# Revit family: TY3332
name_source: partatom
category: Sprinklers
revit_build: Autodesk Revit 2016 (Build: 20150220_1215(x64)
units: mm (PartAtom-declared; Revit-internal decimal feet)

## family parameters
Always vertical = Yes
Cut with Voids When Loaded = No
Maintain Annotation Orientation = No
OmniClass Number = 23.65.70.17.11.24
OmniClass Title = Fire Fighting Sprinkler Heads
Part Type = Normal
Room Calculation Point = No
Round Connector Dimension = Use Diameter
Shared = No
Work Plane-Based = No

## types (15) — shared parameters
COBie = Yes
COBie.Component.Name = Sprinklers:Sidewall_SIN
COBie.Type = Yes
COBie.Type.AssetType = Fixed
COBie.Type.Category = Pr_70_55_97_84:Sprinklers
COBie.Type.Manufacturer = Tyco Fire Protection Products
COBie.Type.Material = Bronze
COBie.Type.NominalHeight = 0' - 0"
COBie.Type.NominalLength = 0' - 0"
COBie.Type.NominalWidth = 0' - 0"
COBie.Type.Shape = Cylinder
COBie.Type.Size = 1/2"(DN15)
COBie.Type.WarrantyGuarantorParts = http://tycofsbp.com
Coverage = Extended
Coverage_ = Extended
K-Factor = 5.5493
Manufacturer = Tyco Fire Protection Products
Manufacturer URL = www.tyco-fire.com
Material_ = Bronze
Model = TY-FRB
Nominal Diameter 1 = 1"
Orifice = Standard
Orifice Size = 0"
Outside Diameter 1 = 1"
Response = Quick
Response_ = Quick
SIN No = TY3332
Takeout 1 = 2"
Technical Data Sheet No = TFP296
zero-valued in all types: COBie.Type.ReplacementCost, Style Id

## per-type parameters (varying)
| type | COBie.Component.Description | COBie.Type.Colour | COBie.Type.DurationUnit | COBie.Type.Finish | COBie.Type.ModelNumber | COBie.Type.ModelReference | Description | Finish_ | Part No | Temperature Rating |
| Horizontal Sidewall Brass 135°F 5.6K ½" NPT_57-376-1-135 | TY-FRB Wet Sidewall  57.2°C K80 DN15 NPT Br | Yellow | year | Natural Brass | 57-376-1-135 | TY-FRB Wet Sidewall  57.2°C K80 DN15 NPT Br | TY-FRB Horizontal Sidewall Brass 135°F 5.6K ½" NPT_57-376-1-135 | Natural Brass | 57-376-1-135 | 135 °F |
| Horizontal Sidewall Brass 155°F 5.6K ½" NPT_57-376-1-155 | TY-FRB Wet Sidewall  68.3°C K80 DN15 NPT Br | Yellow | year | Natural Brass | 57-376-1-155 | TY-FRB Wet Sidewall  68.3°C K80 DN15 NPT Br | TY-FRB Horizontal Sidewall Brass 155°F 5.6K ½" NPT_57-376-1-155 | Natural Brass | 57-376-1-155 | 155 °F |
| Horizontal Sidewall Brass 175°F 5.6K ½" NPT_57-376-1-175 | TY-FRB Wet Sidewall  79.4°C K80 DN15 NPT Br | Yellow | year | Natural Brass | 57-376-1-175 | TY-FRB Wet Sidewall  79.4°C K80 DN15 NPT Br | TY-FRB Horizontal Sidewall Brass 175°F 5.6K ½" NPT_57-376-1-175 | Natural Brass | 57-376-1-175 | 175 °F |
| Horizontal Sidewall White 9010 135°F 5.6K ½" NPT_57-376-3-135 | TY-FRB Wet Sidewall  57.2°C K80 DN15 NPT Wh9010 | White | year | Pure White | 57-376-3-135 | TY-FRB Wet Sidewall  57.2°C K80 DN15 NPT Wh9010 | TY-FRB Horizontal Sidewall White 9010 135°F 5.6K ½" NPT_57-376-3-135 | White RAL9010 | 57-376-3-135 | 135 °F |
| Horizontal Sidewall White 9010 155°F 5.6K ½" NPT_57-376-3-155 | TY-FRB Wet Sidewall  68.3°C K80 DN15 NPT Wh9010 | White |  | Pure White | 57-376-3-155 | TY-FRB Wet Sidewall  68.3°C K80 DN15 NPT Wh9010 | TY-FRB Horizontal Sidewall White 9010 155°F 5.6K ½" NPT_57-376-3-155 | White RAL9010 | 57-376-3-155 | 155 °F |
| Horizontal Sidewall White 9010 175°F 5.6K ½" NPT_57-376-3-175 | TY-FRB Wet Sidewall  79.4°C K80 DN15 NPT Wh9010 | White | year | Pure White | 57-376-3-175 | TY-FRB Wet Sidewall  79.4°C K80 DN15 NPT Wh9010 | TY-FRB Horizontal Sidewall White 9010 175°F 5.6K ½" NPT_57-376-3-175 | White RAL9010 | 57-376-3-175 | 175 °F |
| Horizontal Sidewall White 135°F 5.6K ½" NPT_57-376-4-135 | TY-FRB Wet Sidewall  57.2°C K80 DN15 NPT Wh9003 | White | year | Signal White | 57-376-4-135 | TY-FRB Wet Sidewall  57.2°C K80 DN15 NPT Wh9003 | TY-FRB Horizontal Sidewall White 135°F 5.6K ½" NPT_57-376-4-135 | White RAL9003 | 57-376-4-135 | 135 °F |
| Horizontal Sidewall White 155°F 5.6K ½" NPT_57-376-4-155 | TY-FRB Wet Sidewall  68.3°C K80 DN15 NPT Wh9003 | White | year | Signal White | 57-376-4-155 | TY-FRB Wet Sidewall  68.3°C K80 DN15 NPT Wh9003 | TY-FRB Horizontal Sidewall White 155°F 5.6K ½" NPT_57-376-4-155 | White RAL9003 | 57-376-4-155 | 155 °F |
| Horizontal Sidewall White 175°F 5.6K ½" NPT_57-376-4-175 | TY-FRB Wet Sidewall  79.4°C K80 DN15 NPT Wh9003 | White | year | Signal White | 57-376-4-175 | TY-FRB Wet Sidewall  79.4°C K80 DN15 NPT Wh9003 | TY-FRB Horizontal Sidewall White 175°F 5.6K ½" NPT_57-376-4-175 | White RAL9003 | 57-376-4-175 | 175 °F |
| Horizontal Sidewall Jet Black RAL9005 135°F 5.6K ½" NPT_57-376-5-135 | TY-FRB Wet Sidewall  57.2°C K80 DN15 NPT JBlk | Black | year | Jet Black | 57-376-5-135 | TY-FRB Wet Sidewall  57.2°C K80 DN15 NPT JBlk | TY-FRB Horizontal Sidewall Jet Black RAL9005 135°F 5.6K ½" NPT_57-376-5-135 | Jet Black RAL9005 | 57-376-5-135 | 135 °F |
| Horizontal Sidewall Jet Black RAL9005 155°F 5.6K ½" NPT_57-376-5-155 | TY-FRB Wet Sidewall  68.3°C K80 DN15 NPT JBlk | Black | year | Jet Black | 57-376-5-155 | TY-FRB Wet Sidewall  68.3°C K80 DN15 NPT JBlk | TY-FRB Horizontal Sidewall Jet Black RAL9005 155°F 5.6K ½" NPT_57-376-5-155 | Jet Black RAL9005 | 57-376-5-155 | 155 °F |
| Horizontal Sidewall Jet Black RAL9005 175°F 5.6K ½" NPT_57-376-5-175 | TY-FRB Wet Sidewall  79.4°C K80 DN15 NPT JBlk | Black | year | Jet Black | 57-376-5-175 | TY-FRB Wet Sidewall  79.4°C K80 DN15 NPT JBlk | TY-FRB Horizontal Sidewall Jet Black RAL9005 175°F 5.6K ½" NPT_57-376-5-175 | Jet Black RAL9005 | 57-376-5-175 | 175 °F |
| Horizontal Sidewall Chrome 135°F 5.6K ½" NPT_57-376-9-135 | TY-FRB Wet Sidewall  57.2°C K80 DN15 NPT Chr | Silver | year | Chrome Plated | 57-376-9-135 | TY-FRB Wet Sidewall  57.2°C K80 DN15 NPT Chr | TY-FRB Horizontal Sidewall Chrome 135°F 5.6K ½" NPT_57-376-9-135 | Chrome Plated | 57-376-9-135 | 135 °F |
| Horizontal Sidewall Chrome 155°F 5.6K ½" NPT_57-376-9-155 | TY-FRB Wet Sidewall  68.3°C K80 DN15 NPT Chr | Silver | year | Chrome Plated | 57-376-9-155 | TY-FRB Wet Sidewall  68.3°C K80 DN15 NPT Chr | TY-FRB Horizontal Sidewall Chrome 155°F 5.6K ½" NPT_57-376-9-155 | Chrome Plated | 57-376-9-155 | 155 °F |
| Horizontal Sidewall Chrome 175°F 5.6K ½" NPT_57-376-9-175 | TY-FRB Wet Sidewall  79.4°C K80 DN15 NPT Chr | Silver | year | Chrome plated | 57-376-9-175 | TY-FRB Wet Sidewall  79.4°C K80 DN15 NPT Chr | TY-FRB Horizontal Sidewall Chrome 175°F 5.6K ½" NPT_57-376-9-175 | Chrome Plated | 57-376-9-175 | 175 °F |

## geometry (parser evidence)
native form markers: Blend x6, Sweep x120
no freeform markers — native parametric forms only
